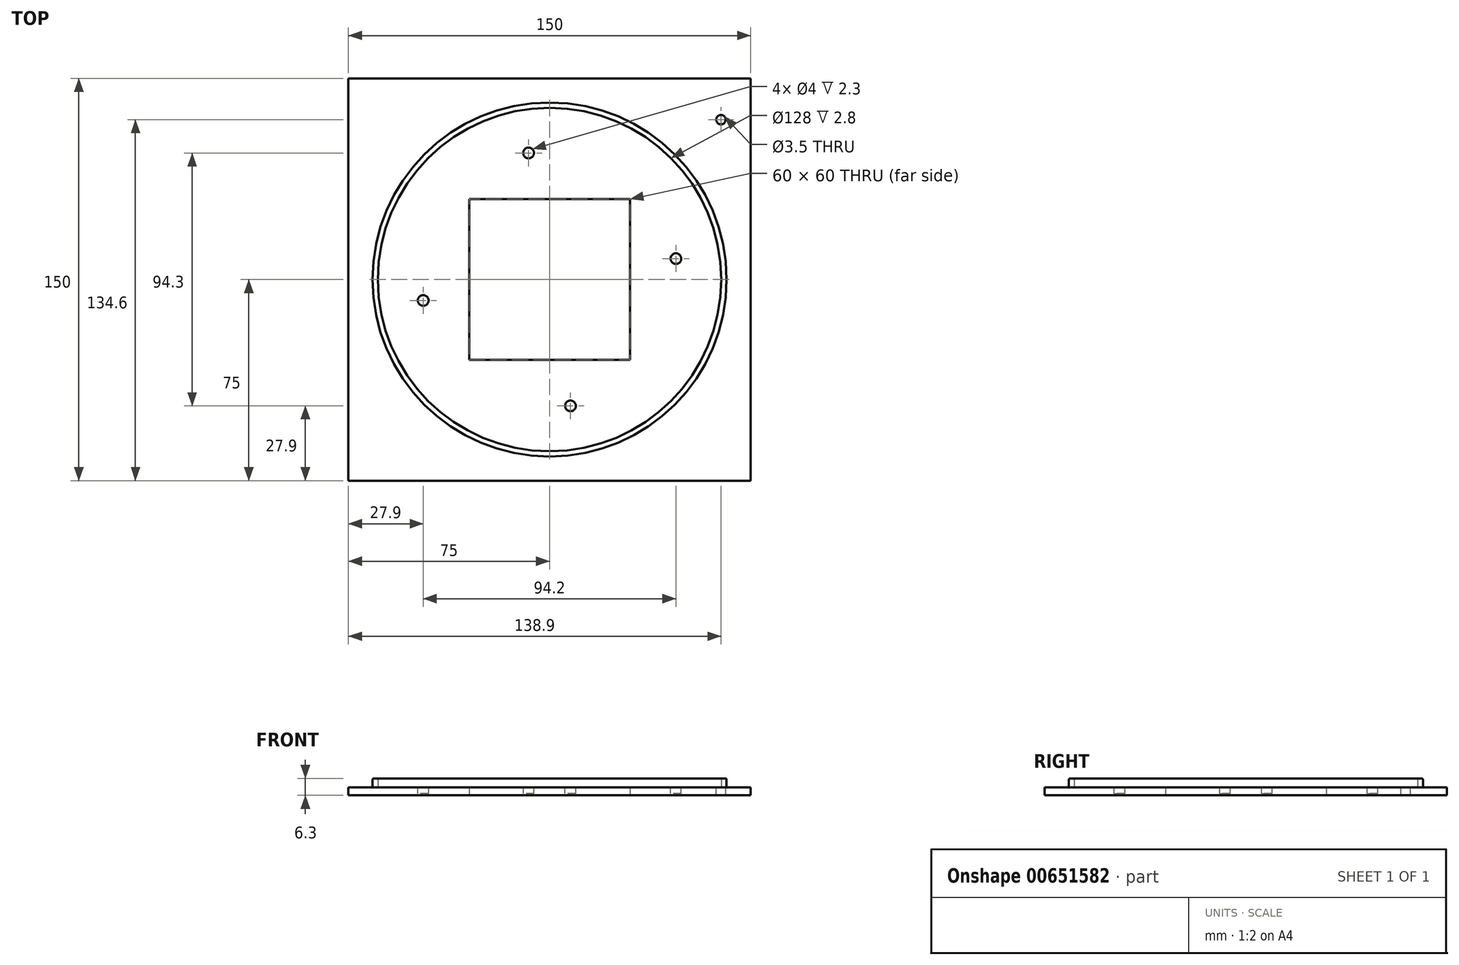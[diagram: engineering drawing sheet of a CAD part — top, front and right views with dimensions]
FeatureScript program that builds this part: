
annotation { "Feature Type Name" : "Feature", "Feature Type Description" : "" }
export const myFeature = defineFeature(function(context is Context, id is Id, definition is map)
    precondition{}
    {
        {
            var Q0;
            Q0=qCreatedBy(makeId("Top.planeOp"),FACE);
            var sketch = newSketch(context, id + "F0", { "sketchPlane" : qUnion([Q0])});
            skLineSegment(sketch, "E0.bottom", {"start": v(75, 75) * mm, "end": v(-75, 75) * mm});
            skLineSegment(sketch, "E0.top", {"start": v(75, -75) * mm, "end": v(-75, -75) * mm});
            skLineSegment(sketch, "E0.left", {"start": v(75, 75) * mm, "end": v(75, -75) * mm});
            skLineSegment(sketch, "E0.right", {"start": v(-75, 75) * mm, "end": v(-75, -75) * mm});
            skPoint(sketch, "E0.middle", {"position": v(0, 0) * mm});
            skLineSegment(sketch, "E1.bottom", {"start": v(30, 30) * mm, "end": v(-30, 30) * mm});
            skLineSegment(sketch, "E1.top", {"start": v(30, -30) * mm, "end": v(-30, -30) * mm});
            skLineSegment(sketch, "E1.left", {"start": v(30, 30) * mm, "end": v(30, -30) * mm});
            skLineSegment(sketch, "E1.right", {"start": v(-30, 30) * mm, "end": v(-30, -30) * mm});
            skSolve(sketch);
        }
        {
            var Q0;
            Q0=makeQuery(id+"F0.imprint","IMPRINT",FACE,{"disambiguationData":[TD([[makeQuery(id+"F0.imprint","IMPRINT",EDGE,{"derivedFrom":sQuery(id+"F0.wireOp",EDGE,"E0.bottom")}),1.0]])]});
            var Q1;
            Q1=makeQuery(id+"F0.imprint","IMPRINT",FACE,{"disambiguationData":[TD([[makeQuery(id+"F0.imprint","IMPRINT",EDGE,{"derivedFrom":sQuery(id+"F0.wireOp",EDGE,"3oa3hqku-FSQT-L0BX-7M5J-21aA9cYNgIiB")}),1.0]])]});
            extrude(context, id + "F1", {"entities" : qUnion([Q0, Q1]), "depth" : 3 * mm});
        }
        {
            var Q0;
            Q0=makeQuery(id+"F1.opExtrude","CAP_FACE",FACE,{"disambiguationData":[OSD([sQuery(id+"F0.wireOp",EDGE,"E0.bottom"),sQuery(id+"F0.wireOp",EDGE,"E0.top"),sQuery(id+"F0.wireOp",EDGE,"E0.left"),sQuery(id+"F0.wireOp",EDGE,"E0.right"),sQuery(id+"F0.wireOp",EDGE,"XZzhmvjU-X5Du-d5F3-4prY-gFx3SX0Bj35v")])],"isStart":false});
            var sketch = newSketch(context, id + "F2", { "sketchPlane" : qUnion([Q0])});
            skCircle(sketch, "E2", {"center": v(0, 0) * mm, "radius": 64 * mm});
            skCircle(sketch, "E3", {"center": v(0, 0) * mm, "radius": 66 * mm});
            skSolve(sketch);
        }
        {
            var Q0;
            Q0=makeQuery(id+"F2.imprint","IMPRINT",FACE,{"disambiguationData":[TD([[makeQuery(id+"F2.imprint","IMPRINT",EDGE,{"derivedFrom":sQuery(id+"F2.wireOp",EDGE,"E2")}),-1.0]])]});
            extrude(context, id + "F3", {"entities" : qUnion([Q0]), "operationType" : NewBodyOperationType.ADD, "depth" : 3.3 * mm});
        }
        {
            var Q0;
            {var subQ0=sQuery(id+"F0.wireOp",EDGE,"E0.right");var subQ1=sQuery(id+"F0.wireOp",EDGE,"E0.left");var subQ2=sQuery(id+"F0.wireOp",EDGE,"E0.top");var subQ3=sQuery(id+"F0.wireOp",EDGE,"WYrh0MW0-zldK-6qiH-74CK-Sv62BQl006fA");var subQ4=sQuery(id+"F0.wireOp",EDGE,"E0.bottom");var subQ5=sQuery(id+"F0.wireOp",EDGE,"WLOIyVNM-Xqk1-ltTo-lkt5-L0Td7G4W8bNn");Q0=makeQuery(id+"F3.boolean.opBoolean","SPLIT",FACE,{"disambiguationData":[TD([makeQuery(id+"F1.opExtrude","SWEPT_FACE",FACE,{"disambiguationData":[OSD([subQ4])]})])],"derivedFrom":makeQuery(id+"F1.opExtrude","CAP_FACE",FACE,{"disambiguationData":[OSD([subQ4,subQ2,subQ1,subQ0,sQuery(id+"F0.wireOp",EDGE,"E1.bottom"),sQuery(id+"F0.wireOp",EDGE,"E1.top"),sQuery(id+"F0.wireOp",EDGE,"E1.left"),sQuery(id+"F0.wireOp",EDGE,"E1.right"),subQ3,subQ5,sQuery(id+"F0.wireOp",EDGE,"nkEUWUvq-pYtE-otFs-pqTU-l5AkutiKREe0")])],"isStart":false})});}
            var sketch = newSketch(context, id + "F4", { "sketchPlane" : qUnion([Q0])});
            skLineSegment(sketch, "E4", {"start": v(-47.1, -75) * mm, "end": v(-47.1, -7.8) * mm});
            skLineSegment(sketch, "E5", {"start": v(-47.1, -7.8) * mm, "end": v(-75, -7.8) * mm});
            skCircle(sketch, "E6", {"center": v(-47.1, -7.8) * mm, "radius": 2 * mm});
            skLineSegment(sketch, "E7", {"start": v(-75, 47.2) * mm, "end": v(-7.8, 47.2) * mm});
            skLineSegment(sketch, "E8", {"start": v(-7.8, 47.2) * mm, "end": v(-7.8, 75) * mm});
            skCircle(sketch, "E9", {"center": v(-7.8, 47.2) * mm, "radius": 2 * mm});
            skLineSegment(sketch, "E10", {"start": v(47.1, 75) * mm, "end": v(47.1, 7.8) * mm});
            skLineSegment(sketch, "E11", {"start": v(47.1, 7.8) * mm, "end": v(75, 7.8) * mm});
            skCircle(sketch, "E12", {"center": v(47.1, 7.8) * mm, "radius": 2 * mm});
            skLineSegment(sketch, "E13", {"start": v(75, -47.1) * mm, "end": v(7.8, -47.1) * mm});
            skLineSegment(sketch, "E14", {"start": v(7.8, -47.1) * mm, "end": v(7.8, -75) * mm});
            skCircle(sketch, "E15", {"center": v(7.8, -47.1) * mm, "radius": 2 * mm});
            skLineSegment(sketch, "E16", {"start": v(63.9, 75) * mm, "end": v(63.9, 59.6) * mm, "construction": true});
            skLineSegment(sketch, "E17", {"start": v(63.9, 59.6) * mm, "end": v(75, 59.6) * mm, "construction": true});
            skCircle(sketch, "E18", {"center": v(63.9, 59.6) * mm, "radius": 1.75 * mm});
            skSolve(sketch);
        }
        {
            var Q0;
            {var subQ0=sQuery(id+"F4.wireOp",EDGE,"83d2e1a0-82d5-4ad9-9520-add51c835ae3");var subQ1=sQuery(id+"F4.wireOp",EDGE,"7fc636ee-dfca-44b1-99cd-784700996732");var subQ2=makeQuery(id+"F4.imprint","INTERSECT",VERTEX,{"derivedFrom":[subQ1,subQ0]});Q0=makeQuery(id+"F4.imprint","IMPRINT",FACE,{"disambiguationData":[TD([[makeQuery(id+"F4.imprint","IMPRINT",EDGE,{"disambiguationData":[TD([[subQ2,1.0]])],"derivedFrom":subQ1}),1.0]])]});}
            var Q1;
            {var subQ0=sQuery(id+"F4.wireOp",EDGE,"83d2e1a0-82d5-4ad9-9520-add51c835ae3");var subQ1=sQuery(id+"F4.wireOp",EDGE,"7fc636ee-dfca-44b1-99cd-784700996732");var subQ2=makeQuery(id+"F4.imprint","INTERSECT",VERTEX,{"derivedFrom":[subQ1,subQ0]});Q1=makeQuery(id+"F4.imprint","IMPRINT",FACE,{"disambiguationData":[TD([[makeQuery(id+"F4.imprint","IMPRINT",EDGE,{"disambiguationData":[TD([[subQ2,1.0]])],"derivedFrom":subQ1}),-1.0]])]});}
            var Q2;
            {var subQ0=sQuery(id+"F4.wireOp",EDGE,"E5");var subQ1=sQuery(id+"F4.wireOp",EDGE,"E4");var subQ2=makeQuery(id+"F4.imprint","INTERSECT",VERTEX,{"derivedFrom":[subQ1,subQ0]});Q2=makeQuery(id+"F4.imprint","IMPRINT",FACE,{"disambiguationData":[TD([[makeQuery(id+"F4.imprint","IMPRINT",EDGE,{"disambiguationData":[TD([[subQ2,1.0]])],"derivedFrom":subQ1}),1.0]])]});}
            var Q3;
            {var subQ0=sQuery(id+"F4.wireOp",EDGE,"E5");var subQ1=sQuery(id+"F4.wireOp",EDGE,"E4");var subQ2=makeQuery(id+"F4.imprint","INTERSECT",VERTEX,{"derivedFrom":[subQ1,subQ0]});Q3=makeQuery(id+"F4.imprint","IMPRINT",FACE,{"disambiguationData":[TD([[makeQuery(id+"F4.imprint","IMPRINT",EDGE,{"disambiguationData":[TD([[subQ2,1.0]])],"derivedFrom":subQ1}),-1.0]])]});}
            var Q4;
            {var subQ0=sQuery(id+"F4.wireOp",EDGE,"E8");var subQ1=sQuery(id+"F4.wireOp",EDGE,"E7");var subQ2=makeQuery(id+"F4.imprint","INTERSECT",VERTEX,{"derivedFrom":[subQ1,subQ0]});Q4=makeQuery(id+"F4.imprint","IMPRINT",FACE,{"disambiguationData":[TD([[makeQuery(id+"F4.imprint","IMPRINT",EDGE,{"disambiguationData":[TD([[subQ2,1.0]])],"derivedFrom":subQ1}),-1.0]])]});}
            var Q5;
            {var subQ0=sQuery(id+"F4.wireOp",EDGE,"E8");var subQ1=sQuery(id+"F4.wireOp",EDGE,"E7");var subQ2=makeQuery(id+"F4.imprint","INTERSECT",VERTEX,{"derivedFrom":[subQ1,subQ0]});Q5=makeQuery(id+"F4.imprint","IMPRINT",FACE,{"disambiguationData":[TD([[makeQuery(id+"F4.imprint","IMPRINT",EDGE,{"disambiguationData":[TD([[subQ2,1.0]])],"derivedFrom":subQ1}),1.0]])]});}
            var Q6;
            {var subQ0=sQuery(id+"F4.wireOp",EDGE,"E11");var subQ1=sQuery(id+"F4.wireOp",EDGE,"E10");var subQ2=makeQuery(id+"F4.imprint","INTERSECT",VERTEX,{"derivedFrom":[subQ1,subQ0]});Q6=makeQuery(id+"F4.imprint","IMPRINT",FACE,{"disambiguationData":[TD([[makeQuery(id+"F4.imprint","IMPRINT",EDGE,{"disambiguationData":[TD([[subQ2,1.0]])],"derivedFrom":subQ1}),-1.0]])]});}
            var Q7;
            {var subQ0=sQuery(id+"F4.wireOp",EDGE,"E11");var subQ1=sQuery(id+"F4.wireOp",EDGE,"E10");var subQ2=makeQuery(id+"F4.imprint","INTERSECT",VERTEX,{"derivedFrom":[subQ1,subQ0]});Q7=makeQuery(id+"F4.imprint","IMPRINT",FACE,{"disambiguationData":[TD([[makeQuery(id+"F4.imprint","IMPRINT",EDGE,{"disambiguationData":[TD([[subQ2,1.0]])],"derivedFrom":subQ1}),1.0]])]});}
            var Q8;
            {var subQ0=sQuery(id+"F4.wireOp",EDGE,"E14");var subQ1=sQuery(id+"F4.wireOp",EDGE,"E13");var subQ2=makeQuery(id+"F4.imprint","INTERSECT",VERTEX,{"derivedFrom":[subQ1,subQ0]});Q8=makeQuery(id+"F4.imprint","IMPRINT",FACE,{"disambiguationData":[TD([[makeQuery(id+"F4.imprint","IMPRINT",EDGE,{"disambiguationData":[TD([[subQ2,1.0]])],"derivedFrom":subQ1}),-1.0]])]});}
            var Q9;
            {var subQ0=sQuery(id+"F4.wireOp",EDGE,"E14");var subQ1=sQuery(id+"F4.wireOp",EDGE,"E13");var subQ2=makeQuery(id+"F4.imprint","INTERSECT",VERTEX,{"derivedFrom":[subQ1,subQ0]});Q9=makeQuery(id+"F4.imprint","IMPRINT",FACE,{"disambiguationData":[TD([[makeQuery(id+"F4.imprint","IMPRINT",EDGE,{"disambiguationData":[TD([[subQ2,1.0]])],"derivedFrom":subQ1}),1.0]])]});}
            extrude(context, id + "F5", {"entities" : qUnion([Q0, Q1, Q2, Q3, Q4, Q5, Q6, Q7, Q8, Q9]), "operationType" : NewBodyOperationType.REMOVE, "oppositeDirection" : true, "depth" : 2.3 * mm});
        }
        {
            var Q0;
            Q0=makeQuery(id+"F3.opExtrude","CAP_EDGE",EDGE,{"disambiguationData":[OSD([sQuery(id+"F2.wireOp",EDGE,"E3")])],"isStart":false});
            fillet(context, id + "F6", {"entities" : qUnion([Q0]), "radius" : 0.5 * mm, "tangentPropagation" : true, "allowEdgeOverflow" : false});
        }
        {
            var Q0;
            Q0=makeQuery(id+"F3.opExtrude","CAP_EDGE",EDGE,{"disambiguationData":[OSD([sQuery(id+"F2.wireOp",EDGE,"E2")])],"isStart":false});
            fillet(context, id + "F7", {"entities" : qUnion([Q0]), "radius" : 0.5 * mm, "tangentPropagation" : true, "allowEdgeOverflow" : false});
        }
        {
            var Q0;
            Q0=makeQuery(id+"F4.imprint","IMPRINT",FACE,{"disambiguationData":[TD([[makeQuery(id+"F4.imprint","IMPRINT",EDGE,{"derivedFrom":sQuery(id+"F4.wireOp",EDGE,"E18")}),1.0]])]});
            extrude(context, id + "F8", {"entities" : qUnion([Q0]), "operationType" : NewBodyOperationType.REMOVE, "oppositeDirection" : true, "depth" : 25 * mm});
        }
    });
